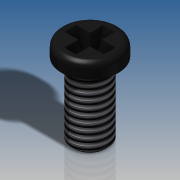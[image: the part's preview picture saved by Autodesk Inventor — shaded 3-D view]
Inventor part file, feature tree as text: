
AUTODESK INVENTOR PART (.ipt)
format: ipt  version: 2016 (Build 200138000, 138)  size: 202,240 bytes
history: native  units: in
note: dims shown in document units (in); Inventor stores cm internally (conversion verified against a paired STEP export)
features: revolve x2, sketch x1, extrude x1, pattern_circular x1, draft x1, thread x1
ambient origin geometry x8: Origin, YZ Plane, XZ Plane, XY Plane, X Axis, Y Axis, Z Axis, Center Point
bodies: Solid1 (feature_tree)
feature tree (7):
  sketch  "Sketch2"  dims[d0=45.0deg d1=0.0079in d2=0.1543in d3=0.0394in d4=0.0157in d5=0.0984in d6=0.1969in d7=90.0deg d8=0.1063in d9=0.0492in d10=60.0deg d11=1.0994in d12=0.0315in d13=0.0in d14=0.7874in d15=90.0deg d17=90.0deg d18=0.2886in d20=0.055in d21=0.3937in d22=0.0in]
  revolve  "Revolution1"  [1 undecoded]
  extrude  "Extrusion1"  Depth=0.3937in
  pattern_circular  "Circular Pattern1"  [2 undecoded]
  revolve  "Revolution2"  [1 undecoded]
  draft  "FaceDraft2"
  thread  "Thread1"  [1 undecoded]
note: 5 required parameter values undecoded (feature->parameter linkage not recoverable at this tier; creation-order binding heuristic only, values carry confidence <= 0.55)